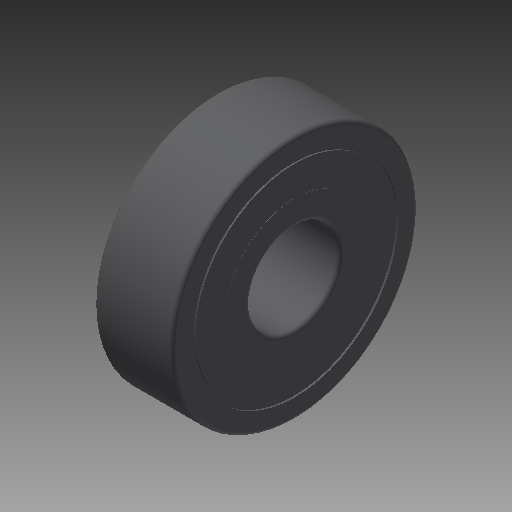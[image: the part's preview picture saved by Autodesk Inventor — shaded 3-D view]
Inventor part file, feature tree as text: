
AUTODESK INVENTOR PART (.ipt)
format: ipt  version: 2018 (Build 220112000, 112)  size: 186,368 bytes
history: native  units: mm
features: other x7, revolve x3, sketch x3
ambient origin geometry x8: Origin, YZ Plane, XZ Plane, XY Plane, X Axis, Y Axis, Z Axis, Center Point
bodies: Solid1 (feature_tree)
feature tree (13):
  revolve  "Revolution1"  Angle=360.0deg
  revolve  "Revolution2"  [1 undecoded]
  revolve  "Revolution3"  [1 undecoded]
  other  "ff_2_XY"
  other  "ff_2_YZ"
  other  "ff_2_ZX"
  other  "ff_2_X"
  other  "ff_2_Y"
  other  "ff_2_Z"
  other  "ff_2_Center"
  sketch  "Sketch_1"  dims[d0=360.0deg d1=360.0deg]
  sketch  "Sketch_2"  dims[d2=360.0deg]
  sketch  "Sketch_3"
note: 2 required parameter values undecoded (feature->parameter linkage not recoverable at this tier; creation-order binding heuristic only, values carry confidence <= 0.55)
